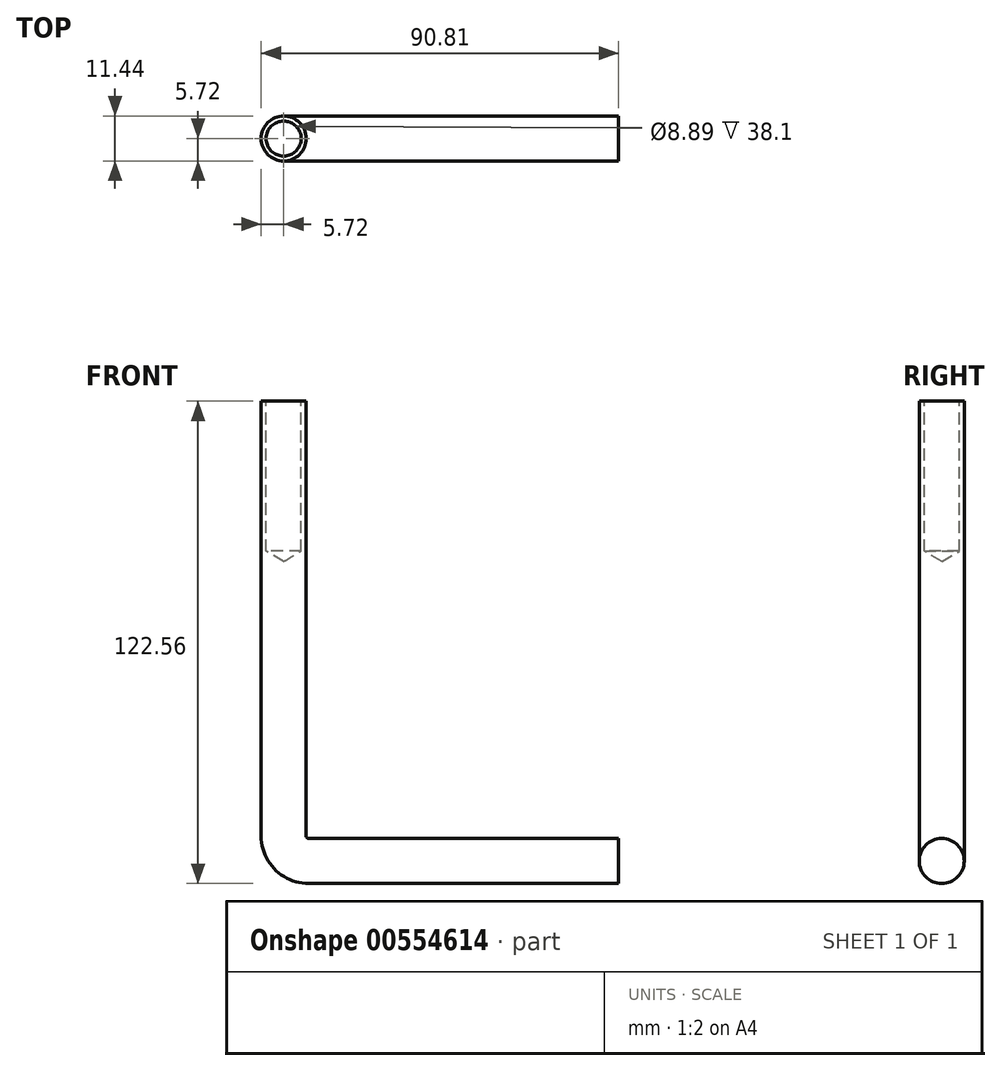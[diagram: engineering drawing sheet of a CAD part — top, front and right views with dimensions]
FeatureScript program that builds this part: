
annotation { "Feature Type Name" : "Feature", "Feature Type Description" : "" }
export const myFeature = defineFeature(function(context is Context, id is Id, definition is map)
    precondition{}
    {
        {
            var Q0;
            Q0=qCreatedBy(makeId("Top.planeOp"),FACE);
            var sketch = newSketch(context, id + "F0", { "sketchPlane" : qUnion([Q0])});
            skCircle(sketch, "E0", {"center": v(0, 0) * mm, "radius": 5.72 * mm});
            skSolve(sketch);
        }
        {
            var Q0;
            Q0=makeQuery(id+"F0.imprint","IMPRINT",FACE,{"disambiguationData":[TD([[makeQuery(id+"F0.imprint","IMPRINT",EDGE,{"derivedFrom":sQuery(id+"F0.wireOp",EDGE,"E0")}),1.0]])]});
            extrude(context, id + "F1", {"entities" : qUnion([Q0]), "depth" : 78.74 * mm});
        }
        {
            var Q0;
            Q0=makeQuery(id+"F1.opExtrude","CAP_FACE",FACE,{"disambiguationData":[OSD([sQuery(id+"F0.wireOp",EDGE,"E0")])],"isStart":false});
            var sketch = newSketch(context, id + "F2", { "sketchPlane" : qUnion([Q0])});
            skPoint(sketch, "E1", {"position": v(0, 0) * mm});
            skSolve(sketch);
        }
        {
            var Q0;
            Q0=sQuery(id+"F2.wireOp",VERTEX,"E1");
            var Q1;
            Q1=makeQuery(id+"F1.opExtrude","SWEPT_BODY",BODY,{"disambiguationData":[OSD([sQuery(id+"F0.wireOp",EDGE,"E0")])]});
            hole(context, id + "F3", {"style" : HoleStyle.SIMPLE, "endStyle" : HoleEndStyle.BLIND, "holeDiameter" : 8.9 * mm, "holeDepth" : 38.1 * mm, "isTappedThrough" : true, "tappedDepth" : 12.7 * mm, "tapClearance" : 3, "locations" : qUnion([Q0]), "scope" : qUnion([Q1]), "majorDiameter" : 6.35 * mm});
        }
        {
            var Q0;
            Q0=makeQuery(id+"F1.opExtrude","CAP_FACE",FACE,{"disambiguationData":[OSD([sQuery(id+"F0.wireOp",EDGE,"E0")])],"isStart":true});
            var sketch = newSketch(context, id + "F4", { "sketchPlane" : qUnion([Q0])});
            skPoint(sketch, "E2", {"position": v(0, 0) * mm});
            skSolve(sketch);
        }
        {
            var Q0;
            Q0=qCreatedBy(makeId("Front.planeOp"),FACE);
            var sketch = newSketch(context, id + "F5", { "sketchPlane" : qUnion([Q0])});
            skLineSegment(sketch, "E3", {"start": v(0, 0) * mm, "end": v(0, -31.75) * mm});
            skLineSegment(sketch, "E4", {"start": v(6.35, -38.1) * mm, "end": v(85.1, -38.1) * mm});
            skPoint(sketch, "E5.visualSharp", {"position": v(0, -38.1) * mm});
            skArc(sketch, "E5.filletArc", {"start": v(0, -31.75) * mm, "mid": v(1.86, -36.24) * mm, "end": v(6.35, -38.1) * mm});
            skSolve(sketch);
        }
        {
            var Q0;
            Q0=makeQuery(id+"F4.imprint","IMPRINT",FACE,{"disambiguationData":[TD([[makeQuery(id+"F4.imprint","IMPRINT",EDGE,{"derivedFrom":makeQuery(id+"F1.opExtrude","CAP_EDGE",EDGE,{"disambiguationData":[OSD([sQuery(id+"F0.wireOp",EDGE,"E0")])],"isStart":true})}),-1.0]])]});
            var Q1;
            Q1=sQuery(id+"F5.wireOp",EDGE,"E3");
            var Q2;
            Q2=sQuery(id+"F5.wireOp",EDGE,"E5.filletArc");
            var Q3;
            Q3=sQuery(id+"F5.wireOp",EDGE,"E4");
            sweep(context, id + "F6", {"operationType" : NewBodyOperationType.ADD, "profiles" : qUnion([Q0]), "path" : qUnion([Q1, Q2, Q3])});
        }
    });
